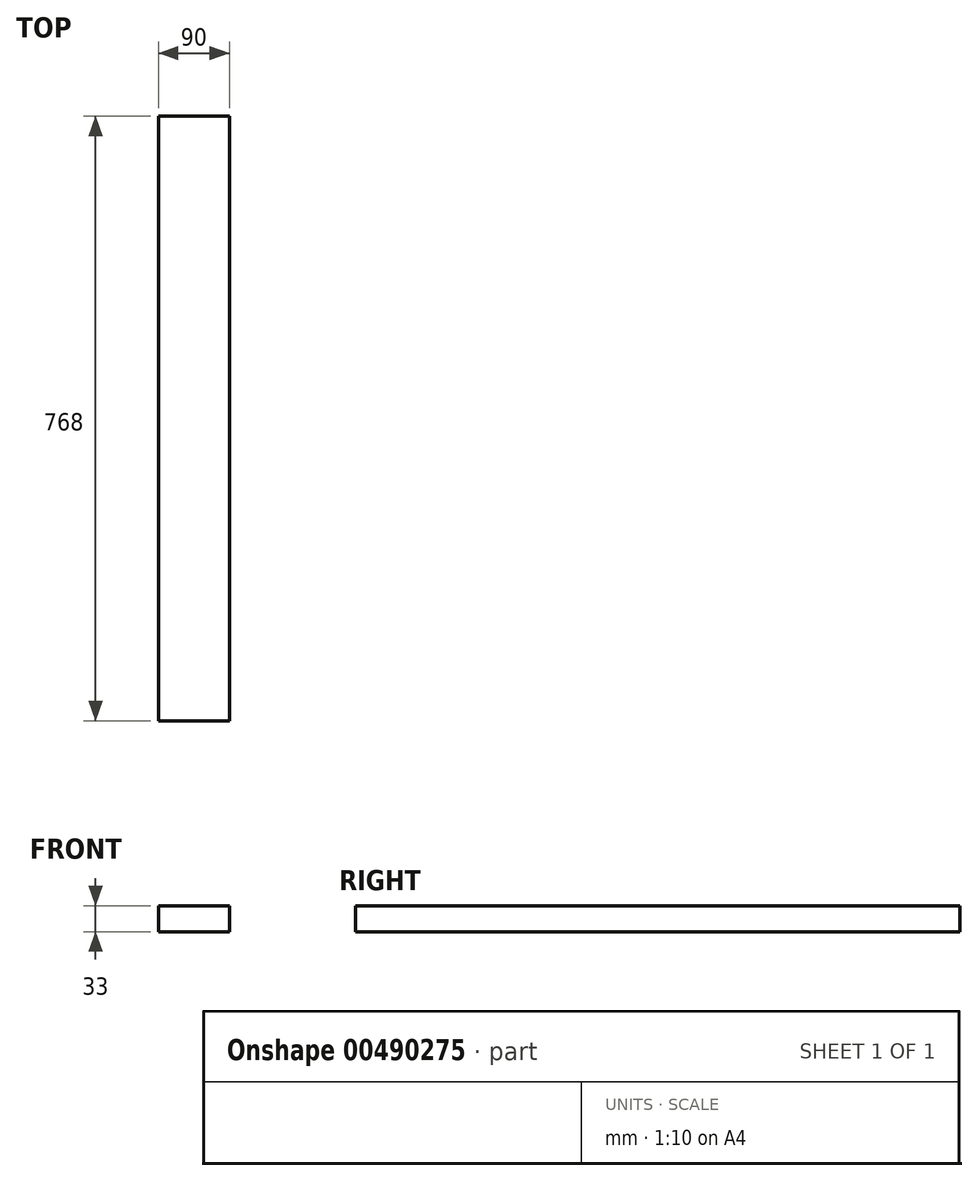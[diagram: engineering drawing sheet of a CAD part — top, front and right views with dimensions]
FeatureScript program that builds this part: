
annotation { "Feature Type Name" : "Feature", "Feature Type Description" : "" }
export const myFeature = defineFeature(function(context is Context, id is Id, definition is map)
    precondition{}
    {
        {
            var Q0;
            Q0=qCreatedBy(makeId("Front.planeOp"),FACE);
            var sketch = newSketch(context, id + "F0", { "sketchPlane" : qUnion([Q0])});
            skLineSegment(sketch, "E0.bottom", {"start": v(0, 0) * mm, "end": v(-90, 0) * mm});
            skLineSegment(sketch, "E0.top", {"start": v(0, 33) * mm, "end": v(-90, 33) * mm});
            skLineSegment(sketch, "E0.left", {"start": v(0, 0) * mm, "end": v(0, 33) * mm});
            skLineSegment(sketch, "E0.right", {"start": v(-90, 0) * mm, "end": v(-90, 33) * mm});
            skSolve(sketch);
        }
        {
            var Q0;
            Q0=makeQuery(id+"F0.imprint","IMPRINT",FACE,{"disambiguationData":[TD([[makeQuery(id+"F0.imprint","IMPRINT",EDGE,{"derivedFrom":sQuery(id+"F0.wireOp",EDGE,"E0.bottom")}),-1.0]])]});
            extrude(context, id + "F1", {"entities" : qUnion([Q0]), "depth" : 768 * mm});
        }
    });
